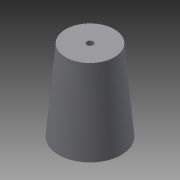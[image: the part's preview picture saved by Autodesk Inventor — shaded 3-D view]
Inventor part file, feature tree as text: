
AUTODESK INVENTOR PART (.ipt)
format: ipt  version: 2013 SP2 (Build 170200200, 200)  size: 94,720 bytes
history: native  units: mm
features: revolve x1
ambient origin geometry x8: Origin, YZ Plane, XZ Plane, XY Plane, X Axis, Y Axis, Z Axis, Center Point
bodies: Solid1 (feature_tree)
feature tree (1):
  revolve  "Revolution1"  [1 undecoded]
note: 1 required parameter value undecoded (feature->parameter linkage not recoverable at this tier; creation-order binding heuristic only, values carry confidence <= 0.55)
